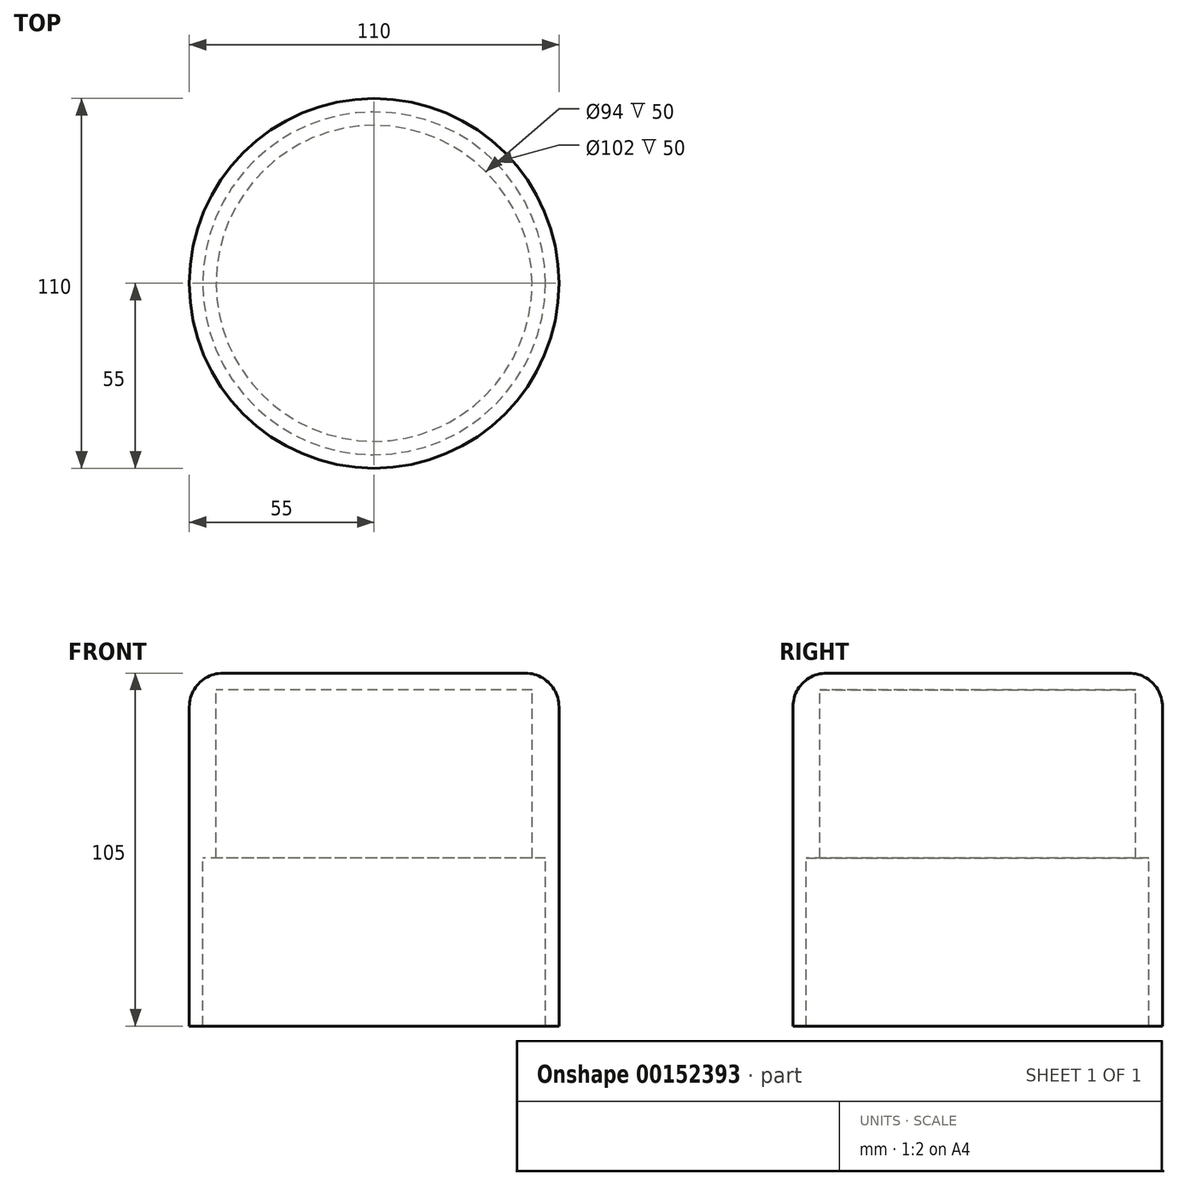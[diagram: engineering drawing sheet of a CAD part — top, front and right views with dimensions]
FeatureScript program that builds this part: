
annotation { "Feature Type Name" : "Feature", "Feature Type Description" : "" }
export const myFeature = defineFeature(function(context is Context, id is Id, definition is map)
    precondition{}
    {
        {
            var Q0;
            Q0=qCreatedBy(makeId("Top.planeOp"),FACE);
            var sketch = newSketch(context, id + "F0", { "sketchPlane" : qUnion([Q0])});
            skCircle(sketch, "E0", {"center": v(0, 0) * mm, "radius": 55 * mm});
            skCircle(sketch, "E1", {"center": v(0, 0) * mm, "radius": 51 * mm});
            skCircle(sketch, "E2", {"center": v(0, 0) * mm, "radius": 47 * mm});
            skSolve(sketch);
        }
        {
            var Q0;
            Q0=makeQuery(id+"F0.imprint","IMPRINT",FACE,{"disambiguationData":[TD([[makeQuery(id+"F0.imprint","IMPRINT",EDGE,{"derivedFrom":sQuery(id+"F0.wireOp",EDGE,"E1")}),1.0]])]});
            var Q1;
            Q1=makeQuery(id+"F0.imprint","IMPRINT",FACE,{"disambiguationData":[TD([[makeQuery(id+"F0.imprint","IMPRINT",EDGE,{"derivedFrom":sQuery(id+"F0.wireOp",EDGE,"E0")}),1.0]])]});
            var Q2;
            Q2=makeQuery(id+"F0.imprint","IMPRINT",FACE,{"disambiguationData":[TD([[makeQuery(id+"F0.imprint","IMPRINT",EDGE,{"derivedFrom":sQuery(id+"F0.wireOp",EDGE,"E2")}),1.0]])]});
            extrude(context, id + "F1", {"entities" : qUnion([Q0, Q1, Q2]), "depth" : 5 * mm});
        }
        {
            var Q0;
            Q0=makeQuery(id+"F0.imprint","IMPRINT",FACE,{"disambiguationData":[TD([[makeQuery(id+"F0.imprint","IMPRINT",EDGE,{"derivedFrom":sQuery(id+"F0.wireOp",EDGE,"E1")}),1.0]])]});
            extrude(context, id + "F2", {"entities" : qUnion([Q0]), "operationType" : NewBodyOperationType.ADD, "oppositeDirection" : true, "depth" : 50 * mm});
        }
        {
            var Q0;
            Q0=makeQuery(id+"F0.imprint","IMPRINT",FACE,{"disambiguationData":[TD([[makeQuery(id+"F0.imprint","IMPRINT",EDGE,{"derivedFrom":sQuery(id+"F0.wireOp",EDGE,"E0")}),1.0]])]});
            extrude(context, id + "F3", {"entities" : qUnion([Q0]), "operationType" : NewBodyOperationType.ADD, "oppositeDirection" : true, "depth" : 100 * mm});
        }
        {
            var Q0;
            Q0=makeQuery(id+"F1.opExtrude","CAP_EDGE",EDGE,{"disambiguationData":[OSD([sQuery(id+"F0.wireOp",EDGE,"E0")])],"isStart":false});
            fillet(context, id + "F4", {"entities" : qUnion([Q0]), "radius" : 10 * mm, "tangentPropagation" : true, "allowEdgeOverflow" : false});
        }
    });
